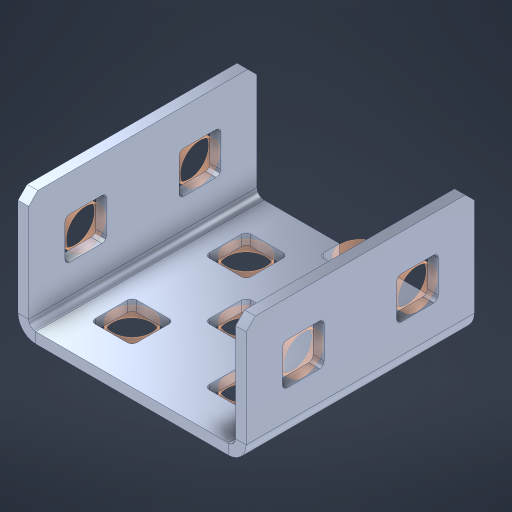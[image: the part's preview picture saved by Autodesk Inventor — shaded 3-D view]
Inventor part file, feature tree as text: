
AUTODESK INVENTOR PART (.ipt)
format: ipt  version: 2023 (Build 270158000, 158)  size: 499,712 bytes
history: native  units: in
note: dims shown in document units (in); Inventor stores cm internally (conversion verified against a paired STEP export)
features: other x17, sheet_metal_op x11, sketch x10, extrude x8, pattern_linear x2, mirror x1, chamfer x1
ambient origin geometry x8: Origin, YZ Plane, XZ Plane, XY Plane, X Axis, Y Axis, Z Axis, Center Point
bodies: Solid1 (feature_tree), Body (feature_tree)
feature tree (50):
  sheet_metal_op  "Flanges"
  other  "Flange Pattern Plane"
  other  "Flange Pattern Sketch"
  sheet_metal_op  "Flange Pattern"
  sheet_metal_op  "Body Pattern"
  pattern_linear  "Center Pattern"  Spacing1=0.0469in  [1 undecoded]
  other  "Arc Length"
  mirror  "Notch Mirror"
  pattern_linear  "Notch Pattern"  Spacing1=0.182in  [1 undecoded]
  chamfer  "End Chamfer"
  extrude  "Half Cut"  Depth=0.02in
  sketch  "Sketch1"  dims[d0=1.0in]
  other  "Plate1"
  sketch  "Sketch2"  dims[d1=1.0in]
  other  "Plate2"
  sheet_metal_op  "Bend1"
  sheet_metal_op  "Corner1"
  sketch  "Sketch3"  dims[d2=0.0469in]
  sketch  "Sketch7"  dims[d3=0.0469in]
  other  "Srf1"
  other  "Srf2"
  sketch  "Sketch8"  dims[d4=0.0234in]
  sketch  "Sketch9"  dims[d5=0.0938in]
  other  "Srf91"
  sheet_metal_op  "Body Pattern Sketch"
  other  "Srf92"
  sketch  "Sketch13"  dims[d6=0.0469in]
  sketch  "Sketch14"  dims[d7=0.5in d8=90.0deg d9=0.0312in]
  sketch  "Sketch15"  dims[d10=0.1875in]
  sketch  "Sketch16"  dims[d11=0.0469in d12=0.0469in d16=0.182in d17=0.02in d18=0.0469in d19=0.0in d20=0.25in d21=0.25in d38=0.7874in d40=0.5in d41=0.7874in d43=1.0in d46=0.172in d47=1.0in d48=0.0in d49=0.182in d50=0.02in d51=0.25in d52=0.25in d53=0.0469in d54=0.0in d55=0.172in d56=1.0in d57=0.0in d58=0.25in d60=0.7874in d62=0.5in d63=0.7874in d65=0.5in d85=0.1227in d86=0.1659in d88=0.04in d89=0.0469in d90=0.0in d91=0.04in d92=0.0491in d95=2.5in d96=0.04in d97=0.25in d98=45.0deg d99=0.25in d100=0.5in d101=0.0in d102=2.497in d106=0.182in d107=0.02in d108=0.5in d109=0.5in d110=0.0469in d111=0.0in d112=0.172in d113=0.5in d114=0.0in d117=0.5in d118=0.5in d119=0.5in]
  other  "Srf786"
  other  "Srf823"
  other  "Srf824"
  other  "Srf856"
  other  "Srf857"
  other  "Srf889"
  sheet_metal_op  "Flange Stamp"
  sheet_metal_op  "Flange Circle"
  sheet_metal_op  "Body Stamp"
  sheet_metal_op  "Body Circle"
  other  "Center Stamp"
  other  "Center Circle"
  sheet_metal_op  "Notch"
  extrude  "ExtrusionSrf2"  Depth=0.0469in
  extrude  "ExtrusionSrf92"  TaperAngle=0.0deg  [1 undecoded]
  extrude  "ExtrusionSrf823"  Depth=0.25in
  extrude  "ExtrusionSrf824"  Depth=0.25in
  extrude  "ExtrusionSrf856"  Depth=0.5in
  extrude  "ExtrusionSrf857"  Depth=0.5in
  extrude  "ExtrusionSrf889"  Depth=1.0in TaperAngle=0.0deg
note: 3 required parameter values undecoded (feature->parameter linkage not recoverable at this tier; creation-order binding heuristic only, values carry confidence <= 0.55)
